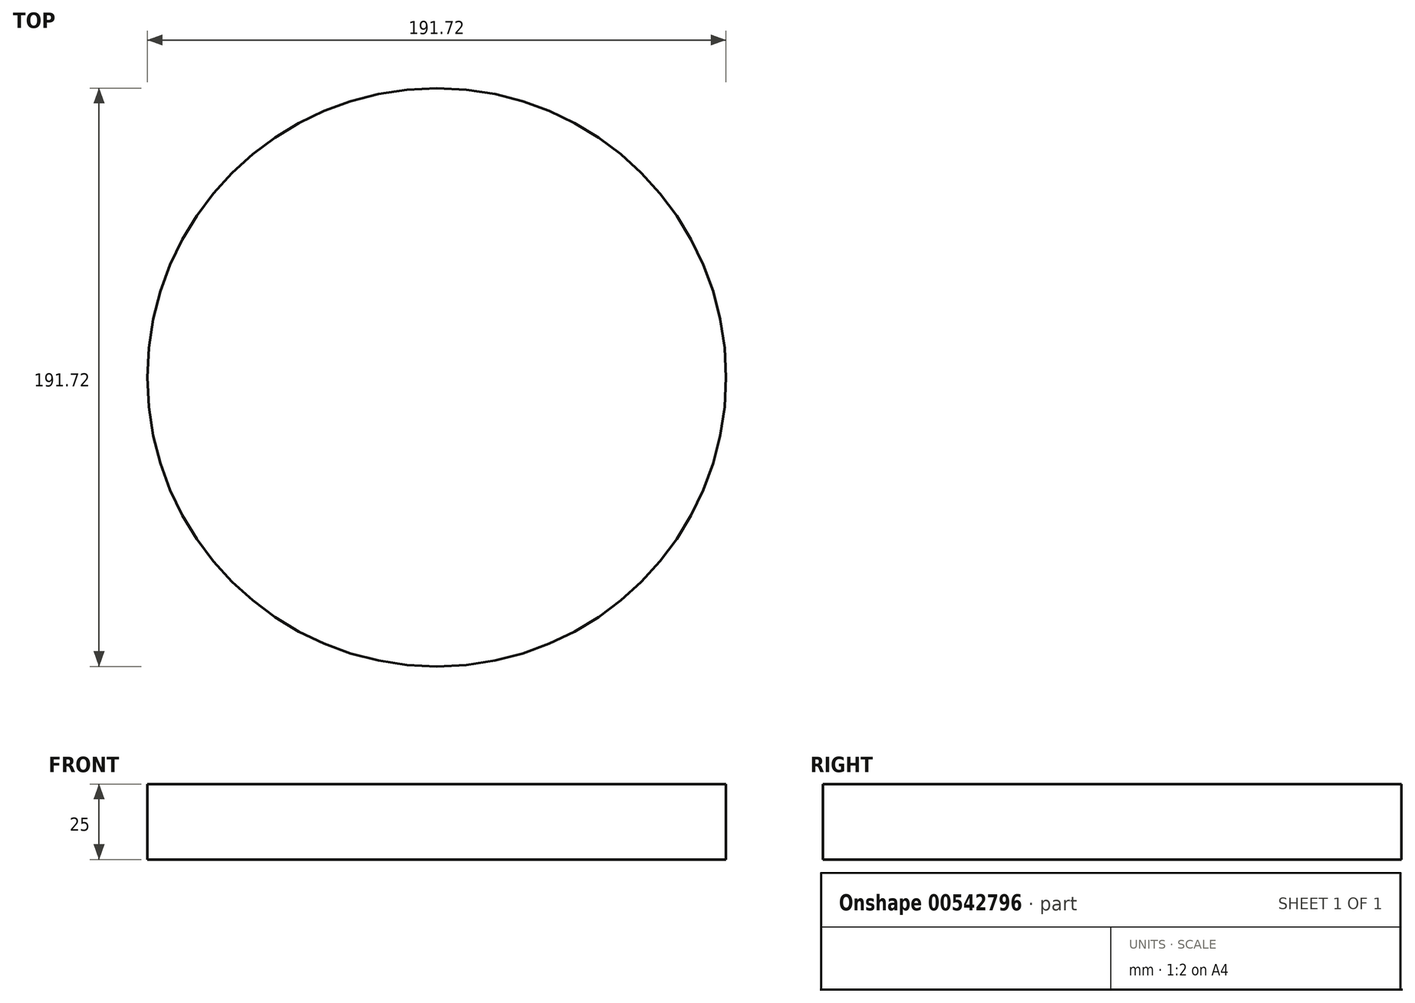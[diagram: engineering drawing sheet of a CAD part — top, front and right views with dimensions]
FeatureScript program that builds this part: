
annotation { "Feature Type Name" : "Feature", "Feature Type Description" : "" }
export const myFeature = defineFeature(function(context is Context, id is Id, definition is map)
    precondition{}
    {
        {
            var Q0;
            Q0=qCreatedBy(makeId("Top.planeOp"),FACE);
            var sketch = newSketch(context, id + "F0", { "sketchPlane" : qUnion([Q0])});
            skCircle(sketch, "E0", {"center": v(0, 0) * mm, "radius": 95.86 * mm});
            skSolve(sketch);
        }
        {
            var Q0;
            Q0=makeQuery(id+"F0.imprint","IMPRINT",FACE,{"disambiguationData":[TD([[makeQuery(id+"F0.imprint","IMPRINT",EDGE,{"derivedFrom":sQuery(id+"F0.wireOp",EDGE,"E0")}),1.0]])]});
            extrude(context, id + "F1", {"entities" : qUnion([Q0]), "depth" : 25 * mm, "offsetDistance" : 25 * mm});
        }
    });
